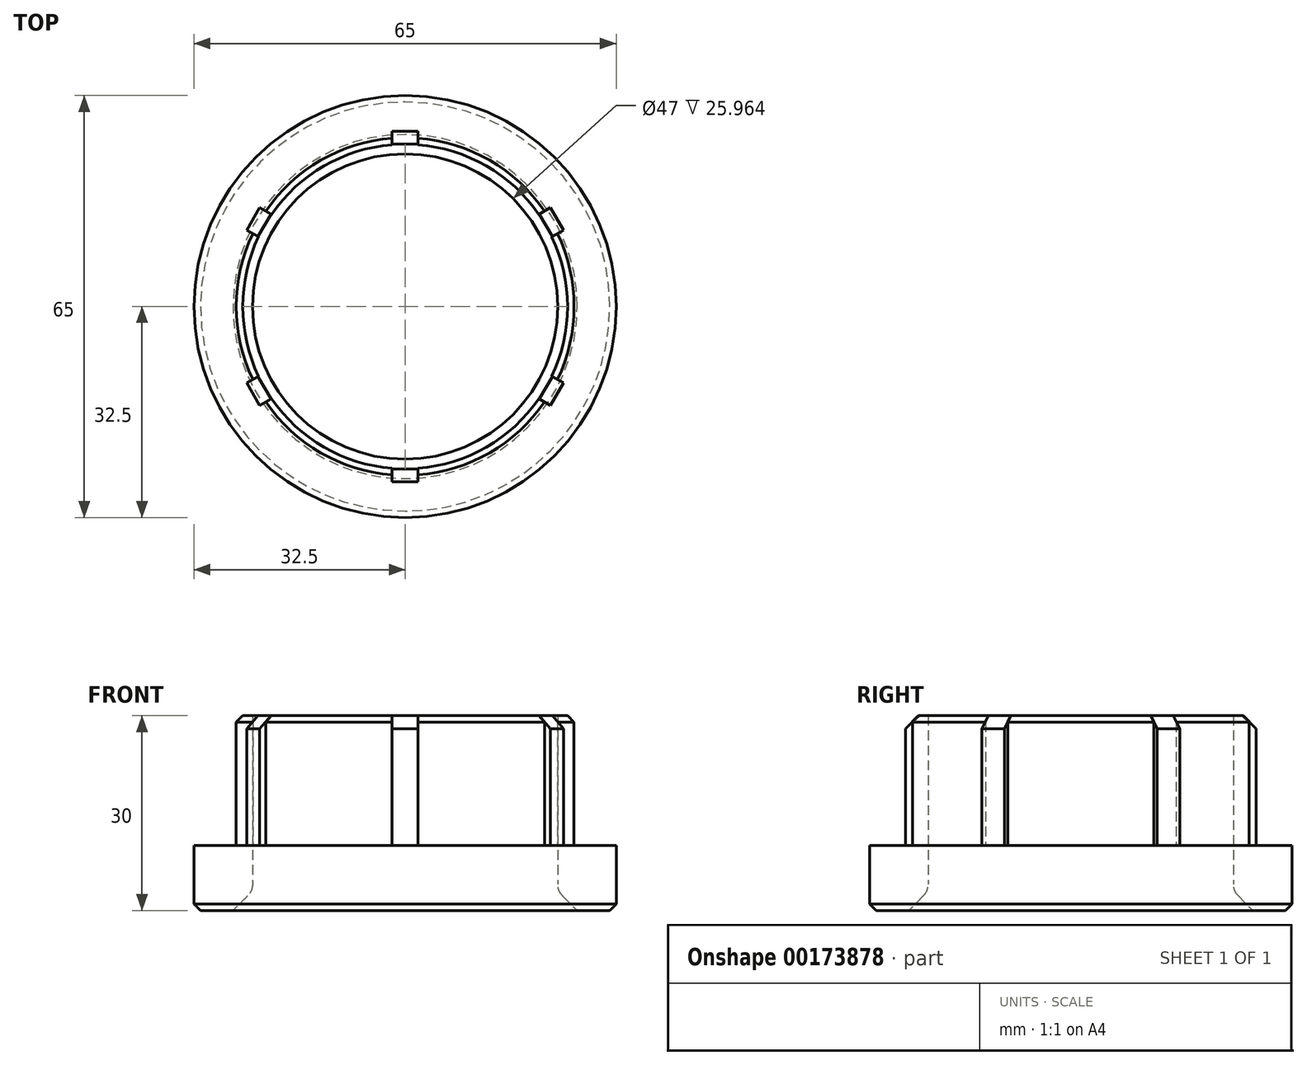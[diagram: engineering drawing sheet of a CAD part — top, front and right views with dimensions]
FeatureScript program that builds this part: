
annotation { "Feature Type Name" : "Feature", "Feature Type Description" : "" }
export const myFeature = defineFeature(function(context is Context, id is Id, definition is map)
    precondition{}
    {
        {
            var Q0;
            Q0=qCreatedBy(makeId("Front.planeOp"),FACE);
            var sketch = newSketch(context, id + "F0", { "sketchPlane" : qUnion([Q0])});
            skLineSegment(sketch, "E0", {"start": v(-23.5, 0) * mm, "end": v(-32.5, 0) * mm});
            skLineSegment(sketch, "E1", {"start": v(-32.5, 0) * mm, "end": v(-32.5, 10) * mm});
            skLineSegment(sketch, "E2", {"start": v(-32.5, 10) * mm, "end": v(-26, 10) * mm});
            skLineSegment(sketch, "E3", {"start": v(-26, 10) * mm, "end": v(-26, 30) * mm});
            skLineSegment(sketch, "E4", {"start": v(-26, 30) * mm, "end": v(-23.5, 30) * mm});
            skLineSegment(sketch, "E5", {"start": v(-23.5, 0) * mm, "end": v(-23.5, 30) * mm});
            skPoint(sketch, "E6.orphan", {"position": v(0, 30) * mm});
            skLineSegment(sketch, "E7", {"start": v(0, 0) * mm, "end": v(0, 54.37) * mm, "construction": true});
            skSolve(sketch);
        }
        {
            var Q0;
            Q0 = qSketchRegion(id + "F0", true);
            var Q1;
            Q1=sQuery(id+"F0.wireOp",EDGE,"E7");
            revolve(context, id + "F1", {"entities" : qUnion([Q0]), "axis" : qUnion([Q1]), "revolveType" : RevolveType.FULL});
        }
        {
            var Q0;
            Q0=makeQuery(id+"F1.opRevolve","SWEPT_EDGE",EDGE,{"disambiguationData":[OSD([sQuery(id+"F0.wireOp",EDGE,"E0"),sQuery(id+"F0.wireOp",EDGE,"E5")])]});
            chamfer(context, id + "F2", {"entities" : qUnion([Q0]), "width" : 3 * mm, "tangentPropagation" : true});
        }
        {
            var Q0;
            {var subQ0=sQuery(id+"F0.wireOp",EDGE,"E5");Q0=makeQuery(id+"F2.opChamfer","BLEND_EDGE",EDGE,{"blendedFrom":[makeQuery(id+"F1.opRevolve","SWEPT_EDGE",EDGE,{"disambiguationData":[OSD([sQuery(id+"F0.wireOp",EDGE,"E0"),subQ0])]}),makeQuery(id+"F1.opRevolve","SWEPT_FACE",FACE,{"disambiguationData":[OSD([subQ0])]})],"blendedInto":[makeQuery(id+"F1.opRevolve","SWEPT_FACE",FACE,{"disambiguationData":[OSD([subQ0])]})]});}
            fillet(context, id + "F3", {"entities" : qUnion([Q0]), "radius" : 2.5 * mm, "tangentPropagation" : true, "allowEdgeOverflow" : false});
        }
        {
            var Q0;
            Q0=makeQuery(id+"F1.opRevolve","SWEPT_FACE",FACE,{"disambiguationData":[OSD([sQuery(id+"F0.wireOp",EDGE,"E4")])]});
            var sketch = newSketch(context, id + "F4", { "sketchPlane" : qUnion([Q0])});
            skLineSegment(sketch, "E8", {"start": v(0, 0) * mm, "end": v(0, -32.5) * mm, "construction": true});
            skLineSegment(sketch, "E9.bottom", {"start": v(2, -25.5) * mm, "end": v(-2, -25.5) * mm});
            skLineSegment(sketch, "E9.top", {"start": v(2, -27) * mm, "end": v(-2, -27) * mm});
            skLineSegment(sketch, "E9.left", {"start": v(2, -25.5) * mm, "end": v(2, -27) * mm});
            skLineSegment(sketch, "E9.right", {"start": v(-2, -25.5) * mm, "end": v(-2, -27) * mm});
            skLineSegment(sketch, "E10", {"start": v(0, 0) * mm, "end": v(-32.5, 0) * mm, "construction": true});
            skLineSegment(sketch, "E11.1.0", {"start": v(24.38, -11.77) * mm, "end": v(22.38, -15.23) * mm});
            skLineSegment(sketch, "E11.1.1", {"start": v(23.08, -11.02) * mm, "end": v(21.08, -14.48) * mm});
            skLineSegment(sketch, "E11.1.2", {"start": v(21.08, -14.48) * mm, "end": v(22.38, -15.23) * mm});
            skLineSegment(sketch, "E11.1.3", {"start": v(23.08, -11.02) * mm, "end": v(24.38, -11.77) * mm});
            skLineSegment(sketch, "E11.2.0", {"start": v(22.38, 15.23) * mm, "end": v(24.38, 11.77) * mm});
            skLineSegment(sketch, "E11.2.1", {"start": v(21.08, 14.48) * mm, "end": v(23.08, 11.02) * mm});
            skLineSegment(sketch, "E11.2.2", {"start": v(23.08, 11.02) * mm, "end": v(24.38, 11.77) * mm});
            skLineSegment(sketch, "E11.2.3", {"start": v(21.08, 14.48) * mm, "end": v(22.38, 15.23) * mm});
            skLineSegment(sketch, "E11.3.0", {"start": v(-2, 27) * mm, "end": v(2, 27) * mm});
            skLineSegment(sketch, "E11.3.1", {"start": v(-2, 25.5) * mm, "end": v(2, 25.5) * mm});
            skLineSegment(sketch, "E11.3.2", {"start": v(2, 25.5) * mm, "end": v(2, 27) * mm});
            skLineSegment(sketch, "E11.3.3", {"start": v(-2, 25.5) * mm, "end": v(-2, 27) * mm});
            skLineSegment(sketch, "E11.4.0", {"start": v(-24.38, 11.77) * mm, "end": v(-22.38, 15.23) * mm});
            skLineSegment(sketch, "E11.4.1", {"start": v(-23.08, 11.02) * mm, "end": v(-21.08, 14.48) * mm});
            skLineSegment(sketch, "E11.4.2", {"start": v(-21.08, 14.48) * mm, "end": v(-22.38, 15.23) * mm});
            skLineSegment(sketch, "E11.4.3", {"start": v(-23.08, 11.02) * mm, "end": v(-24.38, 11.77) * mm});
            skLineSegment(sketch, "E11.5.0", {"start": v(-22.38, -15.23) * mm, "end": v(-24.38, -11.77) * mm});
            skLineSegment(sketch, "E11.5.1", {"start": v(-21.08, -14.48) * mm, "end": v(-23.08, -11.02) * mm});
            skLineSegment(sketch, "E11.5.2", {"start": v(-23.08, -11.02) * mm, "end": v(-24.38, -11.77) * mm});
            skLineSegment(sketch, "E11.5.3", {"start": v(-21.08, -14.48) * mm, "end": v(-22.38, -15.23) * mm});
            skPoint(sketch, "E11.center", {"position": v(0, 0) * mm});
            skSolve(sketch);
        }
        {
            var Q0;
            Q0 = qSketchRegion(id + "F4", true);
            var Q1;
            Q1=makeQuery(id+"F1.opRevolve","SWEPT_FACE",FACE,{"disambiguationData":[OSD([sQuery(id+"F0.wireOp",EDGE,"E2")])]});
            extrude(context, id + "F5", {"entities" : qUnion([Q0]), "operationType" : NewBodyOperationType.ADD, "endBound" : BoundingType.UP_TO_SURFACE, "oppositeDirection" : true, "endBoundEntityFace" : qUnion([Q1]), "depth" : 25 * mm});
        }
        {
            var Q0;
            Q0=makeQuery(id+"F1.opRevolve","SWEPT_EDGE",EDGE,{"disambiguationData":[OSD([sQuery(id+"F0.wireOp",EDGE,"E3"),sQuery(id+"F0.wireOp",EDGE,"E4")])]});
            chamfer(context, id + "F6", {"entities" : qUnion([Q0]), "width" : 1 * mm, "tangentPropagation" : true});
        }
        {
            var Q0;
            Q0=makeQuery(id+"F5.opExtrude","CAP_EDGE",EDGE,{"disambiguationData":[OSD([sQuery(id+"F4.wireOp",EDGE,"E11.1.0")])],"isStart":true});
            var Q1;
            Q1=makeQuery(id+"F5.opExtrude","CAP_EDGE",EDGE,{"disambiguationData":[OSD([sQuery(id+"F4.wireOp",EDGE,"E11.2.0")])],"isStart":true});
            var Q2;
            Q2=makeQuery(id+"F5.opExtrude","CAP_EDGE",EDGE,{"disambiguationData":[OSD([sQuery(id+"F4.wireOp",EDGE,"E11.3.0")])],"isStart":true});
            var Q3;
            Q3=makeQuery(id+"F5.opExtrude","CAP_EDGE",EDGE,{"disambiguationData":[OSD([sQuery(id+"F4.wireOp",EDGE,"E11.4.0")])],"isStart":true});
            var Q4;
            Q4=makeQuery(id+"F5.opExtrude","CAP_EDGE",EDGE,{"disambiguationData":[OSD([sQuery(id+"F4.wireOp",EDGE,"E11.5.0")])],"isStart":true});
            var Q5;
            Q5=makeQuery(id+"F5.opExtrude","CAP_EDGE",EDGE,{"disambiguationData":[OSD([sQuery(id+"F4.wireOp",EDGE,"E9.top")])],"isStart":true});
            chamfer(context, id + "F7", {"entities" : qUnion([Q0, Q1, Q2, Q3, Q4, Q5]), "width" : 2 * mm, "tangentPropagation" : true});
        }
        {
            var Q0;
            Q0=makeQuery(id+"F1.opRevolve","SWEPT_EDGE",EDGE,{"disambiguationData":[OSD([sQuery(id+"F0.wireOp",EDGE,"E0"),sQuery(id+"F0.wireOp",EDGE,"E1")])]});
            chamfer(context, id + "F8", {"entities" : qUnion([Q0]), "width" : 1 * mm, "tangentPropagation" : true});
        }
    });
